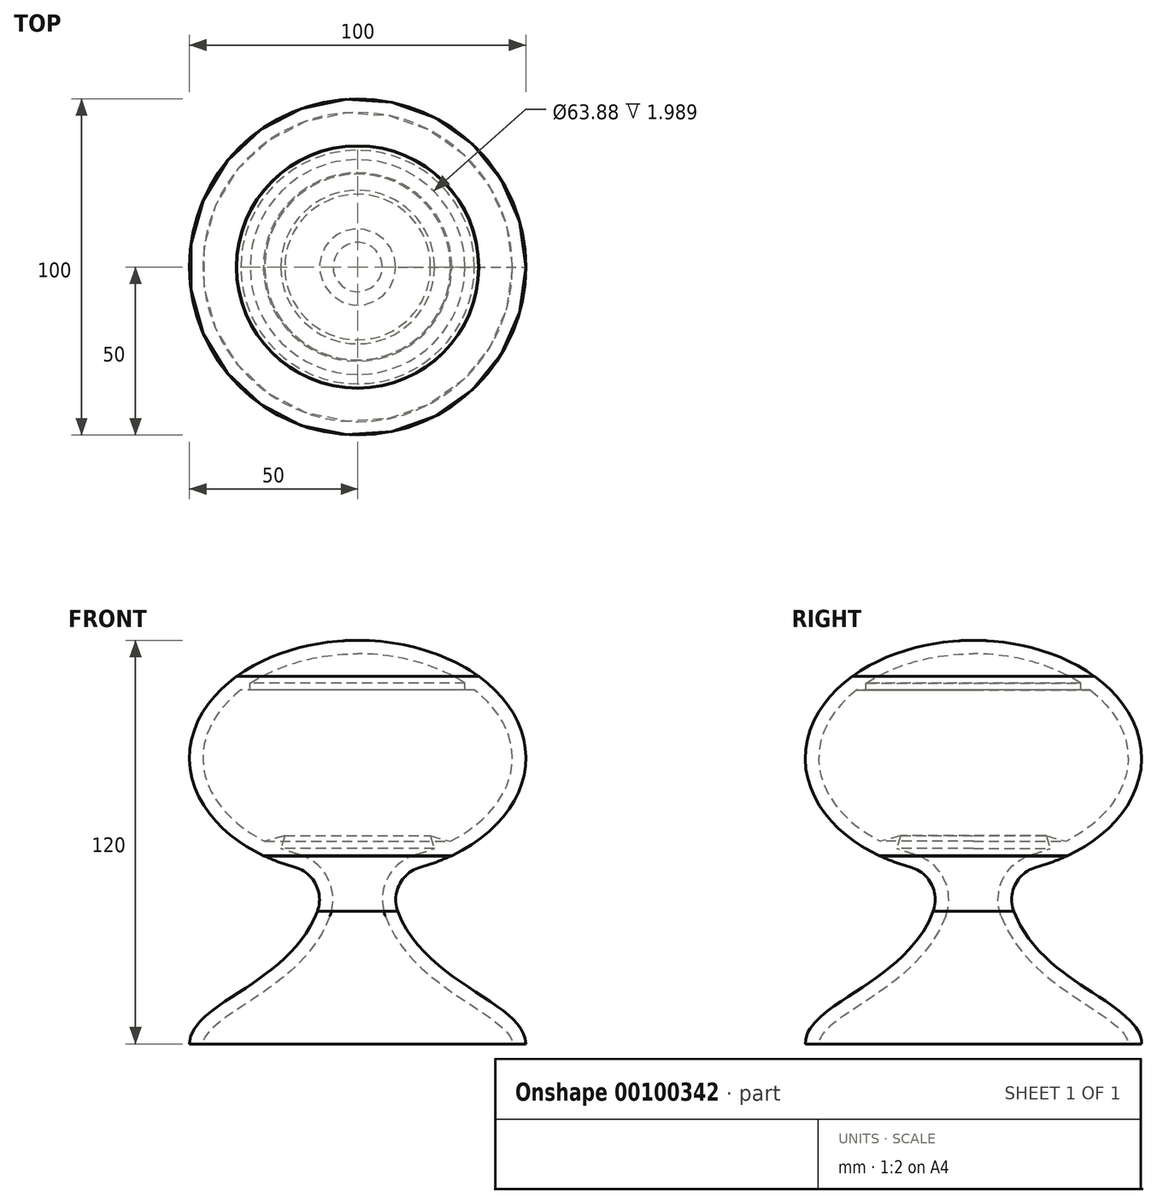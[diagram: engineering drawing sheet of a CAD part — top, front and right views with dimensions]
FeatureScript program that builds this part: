
annotation { "Feature Type Name" : "Feature", "Feature Type Description" : "" }
export const myFeature = defineFeature(function(context is Context, id is Id, definition is map)
    precondition{}
    {
        {
            var Q0;
            Q0=qCreatedBy(makeId("Front.planeOp"),FACE);
            var sketch = newSketch(context, id + "F0", { "sketchPlane" : qUnion([Q0])});
            skLineSegment(sketch, "E0.bottom", {"start": v(50, 50) * mm, "end": v(-50, 50) * mm, "construction": true});
            skLineSegment(sketch, "E0.top", {"start": v(50, 120) * mm, "end": v(-50, 120) * mm, "construction": true});
            skLineSegment(sketch, "E0.left", {"start": v(50, 50) * mm, "end": v(50, 120) * mm, "construction": true});
            skLineSegment(sketch, "E0.right", {"start": v(-50, 50) * mm, "end": v(-50, 120) * mm, "construction": true});
            skPoint(sketch, "E0.middle", {"position": v(0, 85) * mm});
            skEllipticalArc(sketch, "E1", {});
            skLineSegment(sketch, "E2", {"start": v(0, 120) * mm, "end": v(0, 50) * mm});
            skFitSpline(sketch, "E3", {"points": [v(10, 50.7) * mm, v(50, 0) * mm], "startDerivative": vector(0, -94) * mm, "endDerivative": vector(0, -42.42) * mm});
            skLineSegment(sketch, "E4", {"start": v(50, 0) * mm, "end": v(0, 0) * mm});
            skLineSegment(sketch, "E5", {"start": v(0, 0) * mm, "end": v(0, 50) * mm});
            skLineSegment(sketch, "E6", {"start": v(0, 120) * mm, "end": v(4.37, 121.59) * mm});
            skLineSegment(sketch, "E7", {"start": v(4.37, 121.59) * mm, "end": v(6.54, 119.7) * mm});
            skLineSegment(sketch, "E8", {"start": v(6.54, 119.7) * mm, "end": v(12.3, 120) * mm});
            skLineSegment(sketch, "E9", {"start": v(12.3, 120) * mm, "end": v(14.39, 118.52) * mm});
            skLineSegment(sketch, "E10", {"start": v(14.39, 118.52) * mm, "end": v(20.95, 118.52) * mm});
            skLineSegment(sketch, "E11", {"start": v(20.95, 118.52) * mm, "end": v(20.95, 116.78) * mm});
            skLineSegment(sketch, "E12", {"start": v(20.95, 116.78) * mm, "end": v(27.12, 116.78) * mm});
            skLineSegment(sketch, "E13", {"start": v(27.12, 116.78) * mm, "end": v(27.12, 114.4) * mm});
            skLineSegment(sketch, "E14", {"start": v(27.12, 114.4) * mm, "end": v(31.53, 114.18) * mm});
            skLineSegment(sketch, "E15", {"start": v(31.53, 114.18) * mm, "end": v(31.53, 112.16) * mm});
            skLineSegment(sketch, "E16", {"start": v(31.53, 112.16) * mm, "end": v(35.94, 112.16) * mm});
            skLineSegment(sketch, "E17", {"start": v(35.94, 112.16) * mm, "end": v(35.94, 109.24) * mm});
            skLineSegment(sketch, "E18", {"start": v(35.94, 109.24) * mm, "end": v(40.7, 109.24) * mm});
            skLineSegment(sketch, "E19", {"start": v(40.7, 109.24) * mm, "end": v(40.7, 105.33) * mm});
            skLineSegment(sketch, "E20", {"start": v(40.7, 105.33) * mm, "end": v(43.88, 105.33) * mm});
            skLineSegment(sketch, "E21", {"start": v(43.88, 105.33) * mm, "end": v(43.88, 101.78) * mm});
            skLineSegment(sketch, "E22", {"start": v(43.88, 101.78) * mm, "end": v(47.05, 100.42) * mm});
            skLineSegment(sketch, "E23", {"start": v(47.05, 100.42) * mm, "end": v(47.05, 96.84) * mm});
            skLineSegment(sketch, "E24", {"start": v(47.05, 96.84) * mm, "end": v(50, 95.48) * mm});
            skLineSegment(sketch, "E25", {"start": v(50, 95.48) * mm, "end": v(48.75, 92.77) * mm});
            skLineSegment(sketch, "E26", {"start": v(48.75, 92.77) * mm, "end": v(51.46, 91.6) * mm});
            skLineSegment(sketch, "E27", {"start": v(51.46, 91.6) * mm, "end": v(49.84, 87.84) * mm});
            skLineSegment(sketch, "E28", {"start": v(49.84, 87.84) * mm, "end": v(51.81, 85.25) * mm});
            skLineSegment(sketch, "E29", {"start": v(51.81, 85.25) * mm, "end": v(49.97, 83.85) * mm});
            skLineSegment(sketch, "E30", {"start": v(49.97, 83.85) * mm, "end": v(50, 79.61) * mm});
            skLineSegment(sketch, "E31", {"start": v(50, 79.61) * mm, "end": v(48.87, 77.59) * mm});
            skLineSegment(sketch, "E32", {"start": v(48.87, 77.59) * mm, "end": v(50.93, 73.61) * mm});
            skLineSegment(sketch, "E33", {"start": v(50.93, 73.61) * mm, "end": v(45.8, 70.94) * mm});
            skLineSegment(sketch, "E34", {"start": v(45.8, 70.94) * mm, "end": v(45.8, 66.38) * mm});
            skLineSegment(sketch, "E35", {"start": v(45.8, 66.38) * mm, "end": v(42.34, 66.38) * mm});
            skLineSegment(sketch, "E36", {"start": v(42.34, 66.38) * mm, "end": v(44.23, 63.91) * mm});
            skLineSegment(sketch, "E37", {"start": v(44.23, 63.91) * mm, "end": v(39.9, 63.91) * mm});
            skLineSegment(sketch, "E38", {"start": v(39.9, 63.91) * mm, "end": v(39.48, 58.26) * mm});
            skLineSegment(sketch, "E39", {"start": v(39.48, 58.26) * mm, "end": v(35.69, 60.49) * mm});
            skLineSegment(sketch, "E40", {"start": v(35.69, 60.49) * mm, "end": v(37, 56.32) * mm});
            skLineSegment(sketch, "E41", {"start": v(37, 56.32) * mm, "end": v(31.94, 58.07) * mm});
            skLineSegment(sketch, "E42", {"start": v(31.94, 58.07) * mm, "end": v(32.25, 54.87) * mm});
            skLineSegment(sketch, "E43", {"start": v(32.25, 54.87) * mm, "end": v(27.67, 56.1) * mm});
            skLineSegment(sketch, "E44", {"start": v(27.67, 56.1) * mm, "end": v(28.73, 52.76) * mm});
            skLineSegment(sketch, "E45", {"start": v(28.73, 52.76) * mm, "end": v(24.6, 54.53) * mm});
            const initialGuessF0  = {"E1": [0, 0.085, 1, 0, 0.05, 0.035, 4.71238898038469, 1.5707963267948966]};
            skSetInitialGuess(sketch, initialGuessF0);
            skSolve(sketch);
        }
        {
            var Q0;
            Q0=qCreatedBy(makeId("Front.planeOp"),FACE);
            var sketch = newSketch(context, id + "F1", { "sketchPlane" : qUnion([Q0])});
            skLineSegment(sketch, "E46", {"start": v(0, 140.14) * mm, "end": v(0, -55.32) * mm, "construction": true});
            skSolve(sketch);
        }
        {
            var Q0;
            {var subQ11=sQuery(id+"F0.wireOp",EDGE,"E2");Q0=makeQuery(id+"F0.imprint","IMPRINT",FACE,{"disambiguationData":[TD([[makeQuery(id+"F0.imprint","IMPRINT",EDGE,{"derivedFrom":subQ11}),1.0]])]});}
            var Q1;
            {var subQ2=sQuery(id+"F0.wireOp",EDGE,"E3");Q1=makeQuery(id+"F0.imprint","IMPRINT",FACE,{"disambiguationData":[TD([[makeQuery(id+"F0.imprint","IMPRINT",EDGE,{"derivedFrom":subQ2}),-1.0]])]});}
            var Q2;
            Q2=sQuery(id+"F1.wireOp",EDGE,"E46");
            revolve(context, id + "F2", {"entities" : qUnion([Q0, Q1]), "axis" : qUnion([Q2]), "revolveType" : RevolveType.FULL});
        }
        {
            var Q0;
            Q0=makeQuery(id+"F2.opRevolve","SWEPT_EDGE",EDGE,{"disambiguationData":[OSD([sQuery(id+"F0.wireOp",EDGE,"E1"),sQuery(id+"F0.wireOp",EDGE,"E3")])]});
            fillet(context, id + "F3", {"entities" : qUnion([Q0]), "radius" : 10 * mm, "tangentPropagation" : true, "allowEdgeOverflow" : false});
        }
        {
            var Q0;
            Q0=makeQuery(id+"F2.opRevolve","SWEPT_FACE",FACE,{"disambiguationData":[OSD([sQuery(id+"F0.wireOp",EDGE,"E4")])]});
            shell(context, id + "F4", {"entities" : qUnion([Q0]), "thickness" : 4 * mm});
        }
    });
